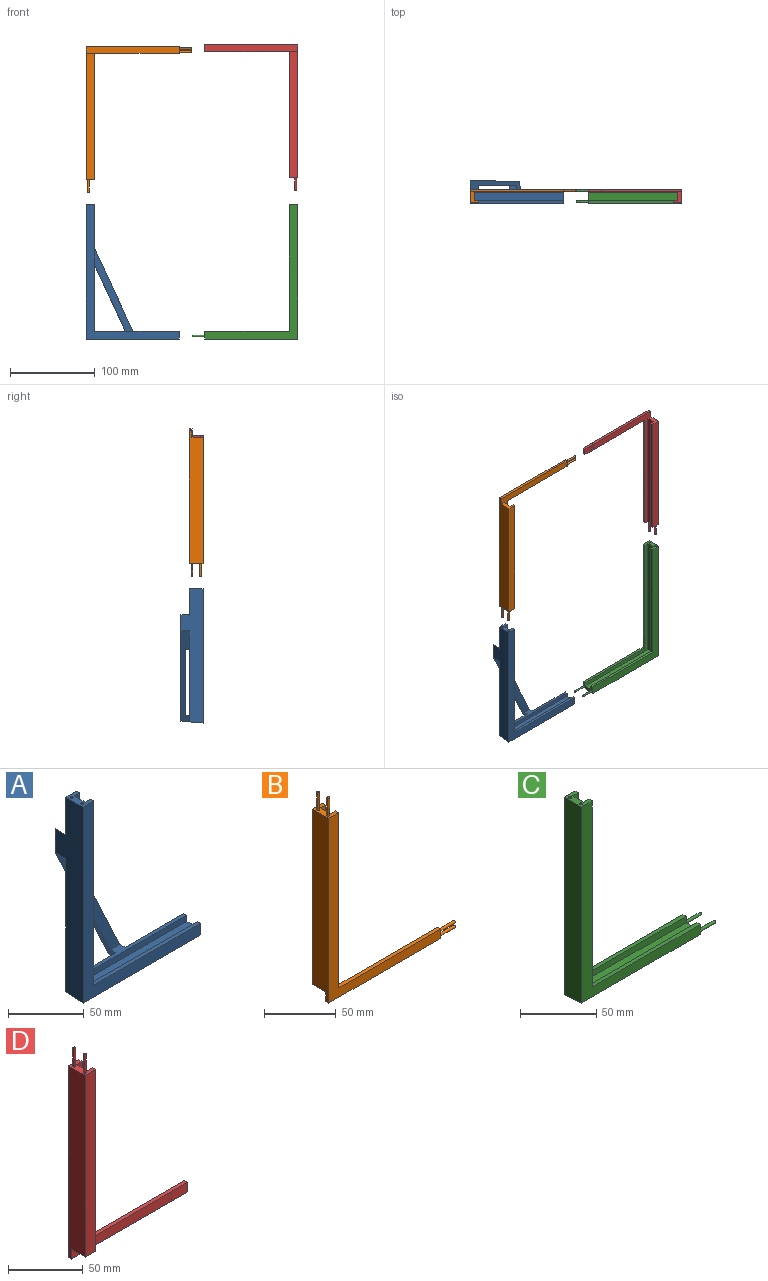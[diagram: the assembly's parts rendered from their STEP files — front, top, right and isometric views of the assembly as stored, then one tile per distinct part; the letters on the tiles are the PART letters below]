
ASSEMBLY  parts=4 mates=3
PART A: 28 faces, bbox 110x26x158.4 mm
  f0: plane 107.35x50.06mm, normal (-0.91,0,-0.42), area 749.9mm2, adj f2,f7,f8,f13,f21,f26,f27
  f1: plane 126.53x59mm, normal (0.91,0,0.42), area 855.7mm2, adj f2,f3,f4,f8,f13,f21,f26,f27
  f2: plane 125.65x58.59mm, normal (0,1,0), area 1037.8mm2, adj f0,f1,f8,f26
  f3: plane 51.92x10mm, normal (0,1,0), area 412mm2, adj f1,f8,f15,f21
  f4: plane 54.73x8mm, normal (0,1,0), area 422.9mm2, adj f1,f10,f13,f26
  f5: plane 100x3mm, normal (0,0,1), area 300mm2, adj f9,f10,f11,f20
  f6: plane 154x105mm, normal (0,-1,0), area 1270mm2, adj f10,f12,f13,f14,f15,f21
  f7: plane 107.35x50.06mm, normal (0,1,0), area 1271.8mm2, adj f0,f8,f13,f21,f26
  f8: plane 158.39x26mm, normal (-1,0,0), area 2714.9mm2, adj f0,f1,f2,f3,f7,f9,f15,f26
  f9: plane 158.39x110mm, normal (0,-1,0), area 2523.4mm2, adj f5,f8,f10,f15,f20,f26
  f10: plane 16x9.39mm, normal (1,0,0), area 82.9mm2, adj f4,f5,f6,f9,f11,f13,f14,f22
  f11: plane 154x105mm, normal (0,1,0), area 1270mm2, adj f5,f10,f12,f14,f15,f20
  f12: plane 154x10mm, normal (1,0,0), area 1540mm2, adj f6,f11,f14,f15
  f13: plane 100x8mm, normal (0,0,1), area 344.7mm2, adj f0,f1,f4,f6,f7,f10,f21,f27
  f14: plane 105x10mm, normal (0,0,1), area 1050mm2, adj f6,f10,f11,f12
  f15: plane 16x10mm, normal (0,0,1), area 103.7mm2, adj f3,f6,f8,f9,f11,f12,f16,f18
  f16: cylinder r=1mm len=15mm, axis (0,0,1), area 94.2mm2, adj f15,f17
  f17: plane 2x2mm, normal (0,0,1), area 3.1mm2, adj f16
  f18: cylinder r=1mm len=15mm, axis (0,0,1), area 94.2mm2, adj f15,f19
  f19: plane 2x2mm, normal (0,0,1), area 3.1mm2, adj f18
  f20: plane 149x3mm, normal (1,0,0), area 447mm2, adj f5,f9,f11,f15
  f21: plane 149x8mm, normal (1,0,0), area 542.9mm2, adj f0,f1,f3,f6,f7,f13,f15,f27
  f22: cylinder r=1mm len=15mm, axis (1,0,0), area 94.2mm2, adj f10,f23
  f23: plane 2x2mm, normal (1,0,0), area 3.1mm2, adj f22
  f24: cylinder r=1mm len=15mm, axis (1,0,0), area 94.2mm2, adj f10,f25
  f25: plane 2x2mm, normal (1,0,0), area 3.1mm2, adj f24
  f26: plane 110x26mm, normal (0,0.09,-1), area 1856.4mm2, adj f0,f1,f2,f4,f7,f8,f9,f10
  f27: plane 97.08x45.27mm, normal (0,-1,0), area 782.3mm2, adj f0,f1,f13,f21
PART B: 21 faces, bbox 125x16x172 mm
  f0: plane 149x10mm, normal (0,1,0), area 1490mm2, adj f1,f9,f15,f20
  f1: plane 157x16mm, normal (-1,0,0), area 2408mm2, adj f0,f2,f6,f7,f9,f20
  f2: plane 110x3mm, normal (0,0,-1), area 330mm2, adj f1,f3,f6,f7
  f3: plane 8x3mm, normal (1,0,0), area 17.7mm2, adj f2,f4,f6,f7,f16,f18
  f4: plane 100x3mm, normal (0,0,1), area 300mm2, adj f3,f6,f7,f14
  f5: plane 149x5mm, normal (0,-1,0), area 745mm2, adj f8,f9,f15,f20
  f6: plane 157x110mm, normal (0,-1,0), area 2370mm2, adj f1,f2,f3,f4,f9,f14
  f7: plane 157x110mm, normal (0,1,0), area 1625mm2, adj f1,f2,f3,f4,f8,f9,f14,f20
  f8: plane 149x10mm, normal (1,0,0), area 1490mm2, adj f5,f7,f9,f20
  f9: plane 16x10mm, normal (0,0,1), area 103.7mm2, adj f0,f1,f5,f6,f7,f8,f10,f12
  f10: cylinder r=1mm len=15mm, axis (0,0,-1), area 94.2mm2, adj f9,f11
  f11: plane 2x2mm, normal (0,0,1), area 3.1mm2, adj f10
  f12: cylinder r=1mm len=15mm, axis (0,0,-1), area 94.2mm2, adj f9,f13
  f13: plane 2x2mm, normal (0,0,1), area 3.1mm2, adj f12
  f14: plane 149x3mm, normal (1,0,0), area 447mm2, adj f4,f6,f7,f9
  f15: plane 149x3mm, normal (1,0,0), area 447mm2, adj f0,f5,f9,f20
  f16: cylinder r=1mm len=15mm, axis (-1,0,0), area 94.2mm2, adj f3,f17
  f17: plane 2x2mm, normal (1,0,0), area 3.1mm2, adj f16
  f18: cylinder r=1mm len=15mm, axis (-1,0,0), area 94.2mm2, adj f3,f19
  f19: plane 2x2mm, normal (1,0,0), area 3.1mm2, adj f18
  f20: plane 13x10mm, normal (0,0,-1), area 80mm2, adj f0,f1,f5,f7,f8,f15
PART C: 22 faces, bbox 125x16x158.4 mm
  f0: plane 100x3mm, normal (0,0,1), area 300mm2, adj f4,f5,f6,f15
  f1: plane 154x105mm, normal (0,-1,0), area 1270mm2, adj f5,f7,f8,f9,f10,f16
  f2: plane 158.39x110mm, normal (0,1,0), area 2523.4mm2, adj f3,f5,f8,f10,f16,f21
  f3: plane 158.39x16mm, normal (-1,0,0), area 2523.2mm2, adj f2,f4,f10,f21
  f4: plane 157x110mm, normal (0,-1,0), area 2370mm2, adj f0,f3,f5,f10,f15,f21
  f5: plane 16x9.39mm, normal (1,0,0), area 82.9mm2, adj f0,f1,f2,f4,f6,f8,f9,f17
  f6: plane 154x105mm, normal (0,1,0), area 1270mm2, adj f0,f5,f7,f9,f10,f15
  f7: plane 154x10mm, normal (1,0,0), area 1540mm2, adj f1,f6,f9,f10
  f8: plane 100x3mm, normal (0,0,1), area 300mm2, adj f1,f2,f5,f16
  f9: plane 105x10mm, normal (0,0,1), area 1050mm2, adj f1,f5,f6,f7
  f10: plane 16x10mm, normal (0,0,1), area 103.7mm2, adj f1,f2,f3,f4,f6,f7,f11,f13
  f11: cylinder r=1mm len=15mm, axis (0,0,1), area 94.2mm2, adj f10,f12
  f12: plane 2x2mm, normal (0,0,1), area 3.1mm2, adj f11
  f13: cylinder r=1mm len=15mm, axis (0,0,1), area 94.2mm2, adj f10,f14
  f14: plane 2x2mm, normal (0,0,1), area 3.1mm2, adj f13
  f15: plane 149x3mm, normal (1,0,0), area 447mm2, adj f0,f4,f6,f10
  f16: plane 149x3mm, normal (1,0,0), area 447mm2, adj f1,f2,f8,f10
  f17: cylinder r=1mm len=15mm, axis (-1,0,0), area 94.2mm2, adj f5,f18
  f18: plane 2x2mm, normal (1,0,0), area 3.1mm2, adj f17
  f19: cylinder r=1mm len=15mm, axis (-1,0,0), area 94.2mm2, adj f5,f20
  f20: plane 2x2mm, normal (1,0,0), area 3.1mm2, adj f19
  f21: plane 110x16mm, normal (0,-0.09,-1), area 1766.7mm2, adj f2,f3,f4,f5
PART D: 21 faces, bbox 110x16x172 mm
  f0: plane 157x16mm, normal (-1,0,0), area 2408mm2, adj f1,f2,f3,f8,f9,f20
  f1: plane 157x110mm, normal (0,-1,0), area 1625mm2, adj f0,f4,f6,f7,f8,f9,f15,f20
  f2: plane 157x110mm, normal (0,1,0), area 2370mm2, adj f0,f4,f7,f8,f9,f15
  f3: plane 149x10mm, normal (0,-1,0), area 1490mm2, adj f0,f9,f14,f20
  f4: plane 8x3mm, normal (1,0,0), area 17.7mm2, adj f1,f2,f7,f8,f16,f18
  f5: plane 149x5mm, normal (0,1,0), area 745mm2, adj f6,f9,f14,f20
  f6: plane 149x10mm, normal (1,0,0), area 1490mm2, adj f1,f5,f9,f20
  f7: plane 100x3mm, normal (0,0,1), area 300mm2, adj f1,f2,f4,f15
  f8: plane 110x3mm, normal (0,0,-1), area 330mm2, adj f0,f1,f2,f4
  f9: plane 16x10mm, normal (0,0,1), area 103.7mm2, adj f0,f1,f2,f3,f5,f6,f10,f12
  f10: cylinder r=1mm len=15mm, axis (0,0,-1), area 94.2mm2, adj f9,f11
  f11: plane 2x2mm, normal (0,0,1), area 3.1mm2, adj f10
  f12: cylinder r=1mm len=15mm, axis (0,0,-1), area 94.2mm2, adj f9,f13
  f13: plane 2x2mm, normal (0,0,1), area 3.1mm2, adj f12
  f14: plane 149x3mm, normal (1,0,0), area 447mm2, adj f3,f5,f9,f20
  f15: plane 149x3mm, normal (1,0,0), area 447mm2, adj f1,f2,f7,f9
  f16: cylinder r=1mm len=15mm, axis (1,0,0), area 94.2mm2, adj f4,f17
  f17: plane 2x2mm, normal (1,0,0), area 3.1mm2, adj f16
  f18: cylinder r=1mm len=15mm, axis (1,0,0), area 94.2mm2, adj f4,f19
  f19: plane 2x2mm, normal (1,0,0), area 3.1mm2, adj f18
  f20: plane 13x10mm, normal (0,0,-1), area 80mm2, adj f0,f1,f3,f5,f6,f14
PLACE A rot(axis=(0.22,-0.33,-0.92),0deg) t=(203.2,12.71,-4.78)mm
PLACE B rot(axis=(-1,0,0),180deg) t=(203.2,12.71,333.22)mm
PLACE C rot(axis=(0,0,1),180deg) t=(343.2,12.71,-4.78)mm
PLACE D rot(axis=(0,1,0),180deg) t=(343.2,12.71,335.22)mm
MATE slider D.f12 <-> C.f13  axis (0,0,-1) through (395.7,7.71,166.22)mm
MATE slider B.f10 <-> A.f16  axis (0,0,-1) through (150.7,7.71,164.22)mm
MATE slider C.f5 <-> A.f10  axis (-1,0,0) through (288.2,12.71,-4.78)mm
